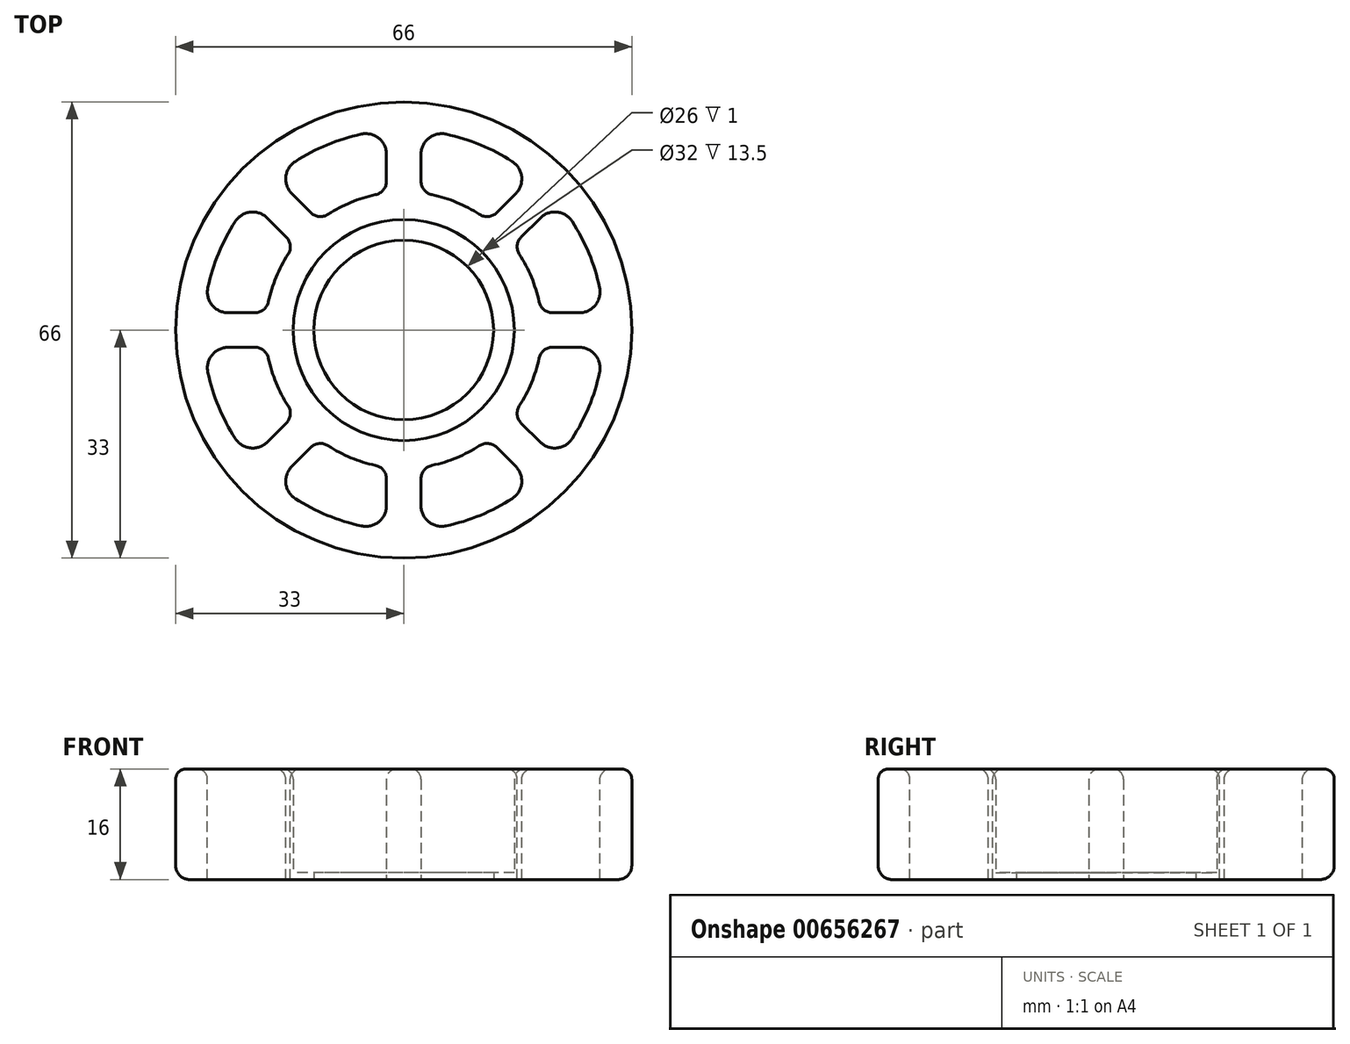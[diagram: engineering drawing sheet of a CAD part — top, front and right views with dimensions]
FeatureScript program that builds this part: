
annotation { "Feature Type Name" : "Feature", "Feature Type Description" : "" }
export const myFeature = defineFeature(function(context is Context, id is Id, definition is map)
    precondition{}
    {
        {
            var Q0;
            Q0=qCreatedBy(makeId("Top.planeOp"),FACE);
            var sketch = newSketch(context, id + "F0", { "sketchPlane" : qUnion([Q0])});
            skCircle(sketch, "E0", {"center": v(0, 0) * mm, "radius": 16 * mm});
            skCircle(sketch, "E1", {"center": v(0, 0) * mm, "radius": 33 * mm});
            skCircle(sketch, "E2", {"center": v(0, 0) * mm, "radius": 13 * mm});
            skSolve(sketch);
        }
        {
            var Q0;
            Q0=makeQuery(id+"F0.imprint","IMPRINT",FACE,{"disambiguationData":[TD([[makeQuery(id+"F0.imprint","IMPRINT",EDGE,{"derivedFrom":sQuery(id+"F0.wireOp",EDGE,"E0")}),1.0]])]});
            extrude(context, id + "F1", {"entities" : qUnion([Q0]), "depth" : 1 * mm, "offsetDistance" : 25 * mm});
        }
        {
            var Q0;
            Q0=makeQuery(id+"F0.imprint","IMPRINT",FACE,{"disambiguationData":[TD([[makeQuery(id+"F0.imprint","IMPRINT",EDGE,{"derivedFrom":sQuery(id+"F0.wireOp",EDGE,"E0")}),-1.0]])]});
            extrude(context, id + "F2", {"entities" : qUnion([Q0]), "operationType" : NewBodyOperationType.ADD, "depth" : 16 * mm, "offsetDistance" : 25 * mm});
        }
        {
            var Q0;
            Q0=makeQuery(id+"F2.opExtrude","CAP_FACE",FACE,{"disambiguationData":[OSD([sQuery(id+"F0.wireOp",EDGE,"E0"),sQuery(id+"F0.wireOp",EDGE,"E1")])],"isStart":false});
            var sketch = newSketch(context, id + "F3", { "sketchPlane" : qUnion([Q0])});
            skLineSegment(sketch, "E3.0", {"start": v(-2.5, 28.9) * mm, "end": v(-2.5, 19.84) * mm});
            skLineSegment(sketch, "E4.0", {"start": v(2.5, 28.9) * mm, "end": v(2.5, 19.84) * mm});
            skCircle(sketch, "E5.0", {"center": v(0, 0) * mm, "radius": 20 * mm});
            skCircle(sketch, "E6.0", {"center": v(0, 0) * mm, "radius": 29 * mm});
            skLineSegment(sketch, "E7.1.0", {"start": v(-22.2, 18.66) * mm, "end": v(-15.8, 12.26) * mm});
            skLineSegment(sketch, "E7.1.1", {"start": v(-18.66, 22.2) * mm, "end": v(-12.26, 15.8) * mm});
            skLineSegment(sketch, "E7.2.0", {"start": v(-28.9, -2.5) * mm, "end": v(-19.84, -2.5) * mm});
            skLineSegment(sketch, "E7.2.1", {"start": v(-28.9, 2.5) * mm, "end": v(-19.84, 2.5) * mm});
            skLineSegment(sketch, "E7.3.0", {"start": v(-18.66, -22.2) * mm, "end": v(-12.26, -15.8) * mm});
            skLineSegment(sketch, "E7.3.1", {"start": v(-22.2, -18.66) * mm, "end": v(-15.8, -12.26) * mm});
            skLineSegment(sketch, "E7.4.0", {"start": v(2.5, -28.9) * mm, "end": v(2.5, -19.84) * mm});
            skLineSegment(sketch, "E7.4.1", {"start": v(-2.5, -28.9) * mm, "end": v(-2.5, -19.84) * mm});
            skLineSegment(sketch, "E7.5.0", {"start": v(22.2, -18.66) * mm, "end": v(15.8, -12.26) * mm});
            skLineSegment(sketch, "E7.5.1", {"start": v(18.66, -22.2) * mm, "end": v(12.26, -15.8) * mm});
            skLineSegment(sketch, "E7.6.0", {"start": v(28.9, 2.5) * mm, "end": v(19.84, 2.5) * mm});
            skLineSegment(sketch, "E7.6.1", {"start": v(28.9, -2.5) * mm, "end": v(19.84, -2.5) * mm});
            skLineSegment(sketch, "E7.7.0", {"start": v(18.66, 22.2) * mm, "end": v(12.26, 15.8) * mm});
            skLineSegment(sketch, "E7.7.1", {"start": v(22.2, 18.66) * mm, "end": v(15.8, 12.26) * mm});
            skSolve(sketch);
        }
        {
            var Q0;
            {var subQ0=sQuery(id+"F3.wireOp",EDGE,"E3.0");Q0=makeQuery(id+"F3.imprint","IMPRINT",FACE,{"disambiguationData":[TD([[makeQuery(id+"F3.imprint","IMPRINT",EDGE,{"derivedFrom":subQ0}),-1.0]])]});}
            var Q1;
            {var subQ0=sQuery(id+"F3.wireOp",EDGE,"E4.0");Q1=makeQuery(id+"F3.imprint","IMPRINT",FACE,{"disambiguationData":[TD([[makeQuery(id+"F3.imprint","IMPRINT",EDGE,{"derivedFrom":subQ0}),1.0]])]});}
            var Q2;
            {var subQ0=sQuery(id+"F3.wireOp",EDGE,"E7.6.0");Q2=makeQuery(id+"F3.imprint","IMPRINT",FACE,{"disambiguationData":[TD([[makeQuery(id+"F3.imprint","IMPRINT",EDGE,{"derivedFrom":subQ0}),-1.0]])]});}
            var Q3;
            {var subQ0=sQuery(id+"F3.wireOp",EDGE,"E7.5.0");Q3=makeQuery(id+"F3.imprint","IMPRINT",FACE,{"disambiguationData":[TD([[makeQuery(id+"F3.imprint","IMPRINT",EDGE,{"derivedFrom":subQ0}),-1.0]])]});}
            var Q4;
            {var subQ0=sQuery(id+"F3.wireOp",EDGE,"E7.4.0");Q4=makeQuery(id+"F3.imprint","IMPRINT",FACE,{"disambiguationData":[TD([[makeQuery(id+"F3.imprint","IMPRINT",EDGE,{"derivedFrom":subQ0}),-1.0]])]});}
            var Q5;
            {var subQ0=sQuery(id+"F3.wireOp",EDGE,"E7.3.0");Q5=makeQuery(id+"F3.imprint","IMPRINT",FACE,{"disambiguationData":[TD([[makeQuery(id+"F3.imprint","IMPRINT",EDGE,{"derivedFrom":subQ0}),-1.0]])]});}
            var Q6;
            {var subQ0=sQuery(id+"F3.wireOp",EDGE,"E7.2.0");Q6=makeQuery(id+"F3.imprint","IMPRINT",FACE,{"disambiguationData":[TD([[makeQuery(id+"F3.imprint","IMPRINT",EDGE,{"derivedFrom":subQ0}),-1.0]])]});}
            var Q7;
            {var subQ0=sQuery(id+"F3.wireOp",EDGE,"E7.1.0");Q7=makeQuery(id+"F3.imprint","IMPRINT",FACE,{"disambiguationData":[TD([[makeQuery(id+"F3.imprint","IMPRINT",EDGE,{"derivedFrom":subQ0}),-1.0]])]});}
            extrude(context, id + "F4", {"entities" : qUnion([Q0, Q1, Q2, Q3, Q4, Q5, Q6, Q7]), "operationType" : NewBodyOperationType.REMOVE, "oppositeDirection" : true, "depth" : 16 * mm, "offsetDistance" : 25 * mm});
        }
        {
            var Q0;
            Q0=makeQuery(id+"F4.boolean.opBoolean","COPY",EDGE,{"derivedFrom":makeQuery(id+"F4.opExtrude","SWEPT_EDGE",EDGE,{"disambiguationData":[OSD([sQuery(id+"F3.wireOp",EDGE,"E6.0"),sQuery(id+"F3.wireOp",EDGE,"E7.1.0")])]})});
            var Q1;
            Q1=makeQuery(id+"F4.boolean.opBoolean","COPY",EDGE,{"derivedFrom":makeQuery(id+"F4.opExtrude","SWEPT_EDGE",EDGE,{"disambiguationData":[OSD([sQuery(id+"F3.wireOp",EDGE,"E4.0"),sQuery(id+"F3.wireOp",EDGE,"E6.0")])]})});
            var Q2;
            Q2=makeQuery(id+"F4.boolean.opBoolean","COPY",EDGE,{"derivedFrom":makeQuery(id+"F4.opExtrude","SWEPT_EDGE",EDGE,{"disambiguationData":[OSD([sQuery(id+"F3.wireOp",EDGE,"E6.0"),sQuery(id+"F3.wireOp",EDGE,"E7.7.1")])]})});
            var Q3;
            Q3=makeQuery(id+"F4.boolean.opBoolean","COPY",EDGE,{"derivedFrom":makeQuery(id+"F4.opExtrude","SWEPT_EDGE",EDGE,{"disambiguationData":[OSD([sQuery(id+"F3.wireOp",EDGE,"E6.0"),sQuery(id+"F3.wireOp",EDGE,"E7.2.0")])]})});
            var Q4;
            Q4=makeQuery(id+"F4.boolean.opBoolean","COPY",EDGE,{"derivedFrom":makeQuery(id+"F4.opExtrude","SWEPT_EDGE",EDGE,{"disambiguationData":[OSD([sQuery(id+"F3.wireOp",EDGE,"E6.0"),sQuery(id+"F3.wireOp",EDGE,"E7.2.1")])]})});
            var Q5;
            Q5=makeQuery(id+"F4.boolean.opBoolean","COPY",EDGE,{"derivedFrom":makeQuery(id+"F4.opExtrude","SWEPT_EDGE",EDGE,{"disambiguationData":[OSD([sQuery(id+"F3.wireOp",EDGE,"E6.0"),sQuery(id+"F3.wireOp",EDGE,"E7.3.1")])]})});
            var Q6;
            Q6=makeQuery(id+"F4.boolean.opBoolean","COPY",EDGE,{"derivedFrom":makeQuery(id+"F4.opExtrude","SWEPT_EDGE",EDGE,{"disambiguationData":[OSD([sQuery(id+"F3.wireOp",EDGE,"E6.0"),sQuery(id+"F3.wireOp",EDGE,"E7.5.0")])]})});
            var Q7;
            Q7=makeQuery(id+"F4.boolean.opBoolean","COPY",EDGE,{"derivedFrom":makeQuery(id+"F4.opExtrude","SWEPT_EDGE",EDGE,{"disambiguationData":[OSD([sQuery(id+"F3.wireOp",EDGE,"E6.0"),sQuery(id+"F3.wireOp",EDGE,"E7.6.0")])]})});
            var Q8;
            Q8=makeQuery(id+"F4.boolean.opBoolean","COPY",EDGE,{"derivedFrom":makeQuery(id+"F4.opExtrude","SWEPT_EDGE",EDGE,{"disambiguationData":[OSD([sQuery(id+"F3.wireOp",EDGE,"E6.0"),sQuery(id+"F3.wireOp",EDGE,"E7.5.1")])]})});
            var Q9;
            Q9=makeQuery(id+"F4.boolean.opBoolean","COPY",EDGE,{"derivedFrom":makeQuery(id+"F4.opExtrude","SWEPT_EDGE",EDGE,{"disambiguationData":[OSD([sQuery(id+"F3.wireOp",EDGE,"E6.0"),sQuery(id+"F3.wireOp",EDGE,"E7.4.1")])]})});
            var Q10;
            Q10=makeQuery(id+"F4.boolean.opBoolean","COPY",EDGE,{"derivedFrom":makeQuery(id+"F4.opExtrude","SWEPT_EDGE",EDGE,{"disambiguationData":[OSD([sQuery(id+"F3.wireOp",EDGE,"E6.0"),sQuery(id+"F3.wireOp",EDGE,"E7.6.1")])]})});
            var Q11;
            Q11=makeQuery(id+"F4.boolean.opBoolean","COPY",EDGE,{"derivedFrom":makeQuery(id+"F4.opExtrude","SWEPT_EDGE",EDGE,{"disambiguationData":[OSD([sQuery(id+"F3.wireOp",EDGE,"E3.0"),sQuery(id+"F3.wireOp",EDGE,"E6.0")])]})});
            var Q12;
            Q12=makeQuery(id+"F4.boolean.opBoolean","COPY",EDGE,{"derivedFrom":makeQuery(id+"F4.opExtrude","SWEPT_EDGE",EDGE,{"disambiguationData":[OSD([sQuery(id+"F3.wireOp",EDGE,"E6.0"),sQuery(id+"F3.wireOp",EDGE,"E7.7.0")])]})});
            var Q13;
            Q13=makeQuery(id+"F4.boolean.opBoolean","COPY",EDGE,{"derivedFrom":makeQuery(id+"F4.opExtrude","SWEPT_EDGE",EDGE,{"disambiguationData":[OSD([sQuery(id+"F3.wireOp",EDGE,"E6.0"),sQuery(id+"F3.wireOp",EDGE,"E7.1.1")])]})});
            var Q14;
            Q14=makeQuery(id+"F4.boolean.opBoolean","COPY",EDGE,{"derivedFrom":makeQuery(id+"F4.opExtrude","SWEPT_EDGE",EDGE,{"disambiguationData":[OSD([sQuery(id+"F3.wireOp",EDGE,"E6.0"),sQuery(id+"F3.wireOp",EDGE,"E7.3.0")])]})});
            var Q15;
            Q15=makeQuery(id+"F4.boolean.opBoolean","COPY",EDGE,{"derivedFrom":makeQuery(id+"F4.opExtrude","SWEPT_EDGE",EDGE,{"disambiguationData":[OSD([sQuery(id+"F3.wireOp",EDGE,"E6.0"),sQuery(id+"F3.wireOp",EDGE,"E7.4.0")])]})});
            fillet(context, id + "F5", {"entities" : qUnion([Q0, Q1, Q2, Q3, Q4, Q5, Q6, Q7, Q8, Q9, Q10, Q11, Q12, Q13, Q14, Q15]), "radius" : 3 * mm, "tangentPropagation" : true, "allowEdgeOverflow" : false});
        }
        {
            var Q0;
            Q0=makeQuery(id+"F4.boolean.opBoolean","COPY",EDGE,{"derivedFrom":makeQuery(id+"F4.opExtrude","SWEPT_EDGE",EDGE,{"disambiguationData":[OSD([sQuery(id+"F3.wireOp",EDGE,"E5.0"),sQuery(id+"F3.wireOp",EDGE,"E7.3.1")])]})});
            var Q1;
            Q1=makeQuery(id+"F4.boolean.opBoolean","COPY",EDGE,{"derivedFrom":makeQuery(id+"F4.opExtrude","SWEPT_EDGE",EDGE,{"disambiguationData":[OSD([sQuery(id+"F3.wireOp",EDGE,"E5.0"),sQuery(id+"F3.wireOp",EDGE,"E7.2.1")])]})});
            var Q2;
            Q2=makeQuery(id+"F4.boolean.opBoolean","COPY",EDGE,{"derivedFrom":makeQuery(id+"F4.opExtrude","SWEPT_EDGE",EDGE,{"disambiguationData":[OSD([sQuery(id+"F3.wireOp",EDGE,"E3.0"),sQuery(id+"F3.wireOp",EDGE,"E5.0")])]})});
            var Q3;
            Q3=makeQuery(id+"F4.boolean.opBoolean","COPY",EDGE,{"derivedFrom":makeQuery(id+"F4.opExtrude","SWEPT_EDGE",EDGE,{"disambiguationData":[OSD([sQuery(id+"F3.wireOp",EDGE,"E5.0"),sQuery(id+"F3.wireOp",EDGE,"E7.1.1")])]})});
            var Q4;
            Q4=makeQuery(id+"F4.boolean.opBoolean","COPY",EDGE,{"derivedFrom":makeQuery(id+"F4.opExtrude","SWEPT_EDGE",EDGE,{"disambiguationData":[OSD([sQuery(id+"F3.wireOp",EDGE,"E4.0"),sQuery(id+"F3.wireOp",EDGE,"E5.0")])]})});
            var Q5;
            Q5=makeQuery(id+"F4.boolean.opBoolean","COPY",EDGE,{"derivedFrom":makeQuery(id+"F4.opExtrude","SWEPT_EDGE",EDGE,{"disambiguationData":[OSD([sQuery(id+"F3.wireOp",EDGE,"E5.0"),sQuery(id+"F3.wireOp",EDGE,"E7.6.0")])]})});
            var Q6;
            Q6=makeQuery(id+"F4.boolean.opBoolean","COPY",EDGE,{"derivedFrom":makeQuery(id+"F4.opExtrude","SWEPT_EDGE",EDGE,{"disambiguationData":[OSD([sQuery(id+"F3.wireOp",EDGE,"E5.0"),sQuery(id+"F3.wireOp",EDGE,"E7.2.0")])]})});
            var Q7;
            Q7=makeQuery(id+"F4.boolean.opBoolean","COPY",EDGE,{"derivedFrom":makeQuery(id+"F4.opExtrude","SWEPT_EDGE",EDGE,{"disambiguationData":[OSD([sQuery(id+"F3.wireOp",EDGE,"E5.0"),sQuery(id+"F3.wireOp",EDGE,"E7.3.0")])]})});
            var Q8;
            Q8=makeQuery(id+"F4.boolean.opBoolean","COPY",EDGE,{"derivedFrom":makeQuery(id+"F4.opExtrude","SWEPT_EDGE",EDGE,{"disambiguationData":[OSD([sQuery(id+"F3.wireOp",EDGE,"E5.0"),sQuery(id+"F3.wireOp",EDGE,"E7.4.1")])]})});
            var Q9;
            Q9=makeQuery(id+"F4.boolean.opBoolean","COPY",EDGE,{"derivedFrom":makeQuery(id+"F4.opExtrude","SWEPT_EDGE",EDGE,{"disambiguationData":[OSD([sQuery(id+"F3.wireOp",EDGE,"E5.0"),sQuery(id+"F3.wireOp",EDGE,"E7.5.1")])]})});
            var Q10;
            Q10=makeQuery(id+"F4.boolean.opBoolean","COPY",EDGE,{"derivedFrom":makeQuery(id+"F4.opExtrude","SWEPT_EDGE",EDGE,{"disambiguationData":[OSD([sQuery(id+"F3.wireOp",EDGE,"E5.0"),sQuery(id+"F3.wireOp",EDGE,"E7.4.0")])]})});
            var Q11;
            Q11=makeQuery(id+"F4.boolean.opBoolean","COPY",EDGE,{"derivedFrom":makeQuery(id+"F4.opExtrude","SWEPT_EDGE",EDGE,{"disambiguationData":[OSD([sQuery(id+"F3.wireOp",EDGE,"E5.0"),sQuery(id+"F3.wireOp",EDGE,"E7.5.0")])]})});
            var Q12;
            Q12=makeQuery(id+"F4.boolean.opBoolean","COPY",EDGE,{"derivedFrom":makeQuery(id+"F4.opExtrude","SWEPT_EDGE",EDGE,{"disambiguationData":[OSD([sQuery(id+"F3.wireOp",EDGE,"E5.0"),sQuery(id+"F3.wireOp",EDGE,"E7.7.0")])]})});
            var Q13;
            Q13=makeQuery(id+"F4.boolean.opBoolean","COPY",EDGE,{"derivedFrom":makeQuery(id+"F4.opExtrude","SWEPT_EDGE",EDGE,{"disambiguationData":[OSD([sQuery(id+"F3.wireOp",EDGE,"E5.0"),sQuery(id+"F3.wireOp",EDGE,"E7.1.0")])]})});
            var Q14;
            Q14=makeQuery(id+"F4.boolean.opBoolean","COPY",EDGE,{"derivedFrom":makeQuery(id+"F4.opExtrude","SWEPT_EDGE",EDGE,{"disambiguationData":[OSD([sQuery(id+"F3.wireOp",EDGE,"E5.0"),sQuery(id+"F3.wireOp",EDGE,"E7.6.1")])]})});
            var Q15;
            Q15=makeQuery(id+"F4.boolean.opBoolean","COPY",EDGE,{"derivedFrom":makeQuery(id+"F4.opExtrude","SWEPT_EDGE",EDGE,{"disambiguationData":[OSD([sQuery(id+"F3.wireOp",EDGE,"E5.0"),sQuery(id+"F3.wireOp",EDGE,"E7.7.1")])]})});
            fillet(context, id + "F6", {"entities" : qUnion([Q0, Q1, Q2, Q3, Q4, Q5, Q6, Q7, Q8, Q9, Q10, Q11, Q12, Q13, Q14, Q15]), "radius" : 2 * mm, "tangentPropagation" : true, "allowEdgeOverflow" : false});
        }
        {
            var Q0;
            Q0=makeQuery(id+"F2.opExtrude","CAP_FACE",FACE,{"disambiguationData":[OSD([sQuery(id+"F0.wireOp",EDGE,"E0"),sQuery(id+"F0.wireOp",EDGE,"E1")])],"isStart":false});
            fillet(context, id + "F7", {"entities" : qUnion([Q0]), "radius" : 1.5 * mm, "tangentPropagation" : true, "allowEdgeOverflow" : false});
        }
        {
            var Q0;
            Q0=makeQuery(id+"F2.opExtrude","CAP_EDGE",EDGE,{"disambiguationData":[OSD([sQuery(id+"F0.wireOp",EDGE,"E1")])],"isStart":true});
            fillet(context, id + "F8", {"entities" : qUnion([Q0]), "radius" : 2 * mm, "tangentPropagation" : true, "allowEdgeOverflow" : false});
        }
    });
